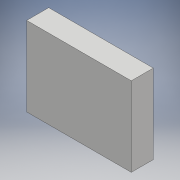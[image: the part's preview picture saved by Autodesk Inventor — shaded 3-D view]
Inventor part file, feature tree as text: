
AUTODESK INVENTOR PART (.ipt)
format: ipt  version: 2018.1 (Build 221171000, 171)  size: 92,160 bytes
history: native  units: mm
features: other x1, extrude x1, shell x1, sketch x1
ambient origin geometry x8: Origin, YZ Plane, XZ Plane, XY Plane, X Axis, Y Axis, Z Axis, Center Point
bodies: Body1 (feature_tree)
feature tree (4):
  other  "ソリッド1"
  extrude  "押し出し1"  Depth=95.0mm
  shell  "シェル1"  Thickness=72.0mm
  sketch  "スケッチ1"
